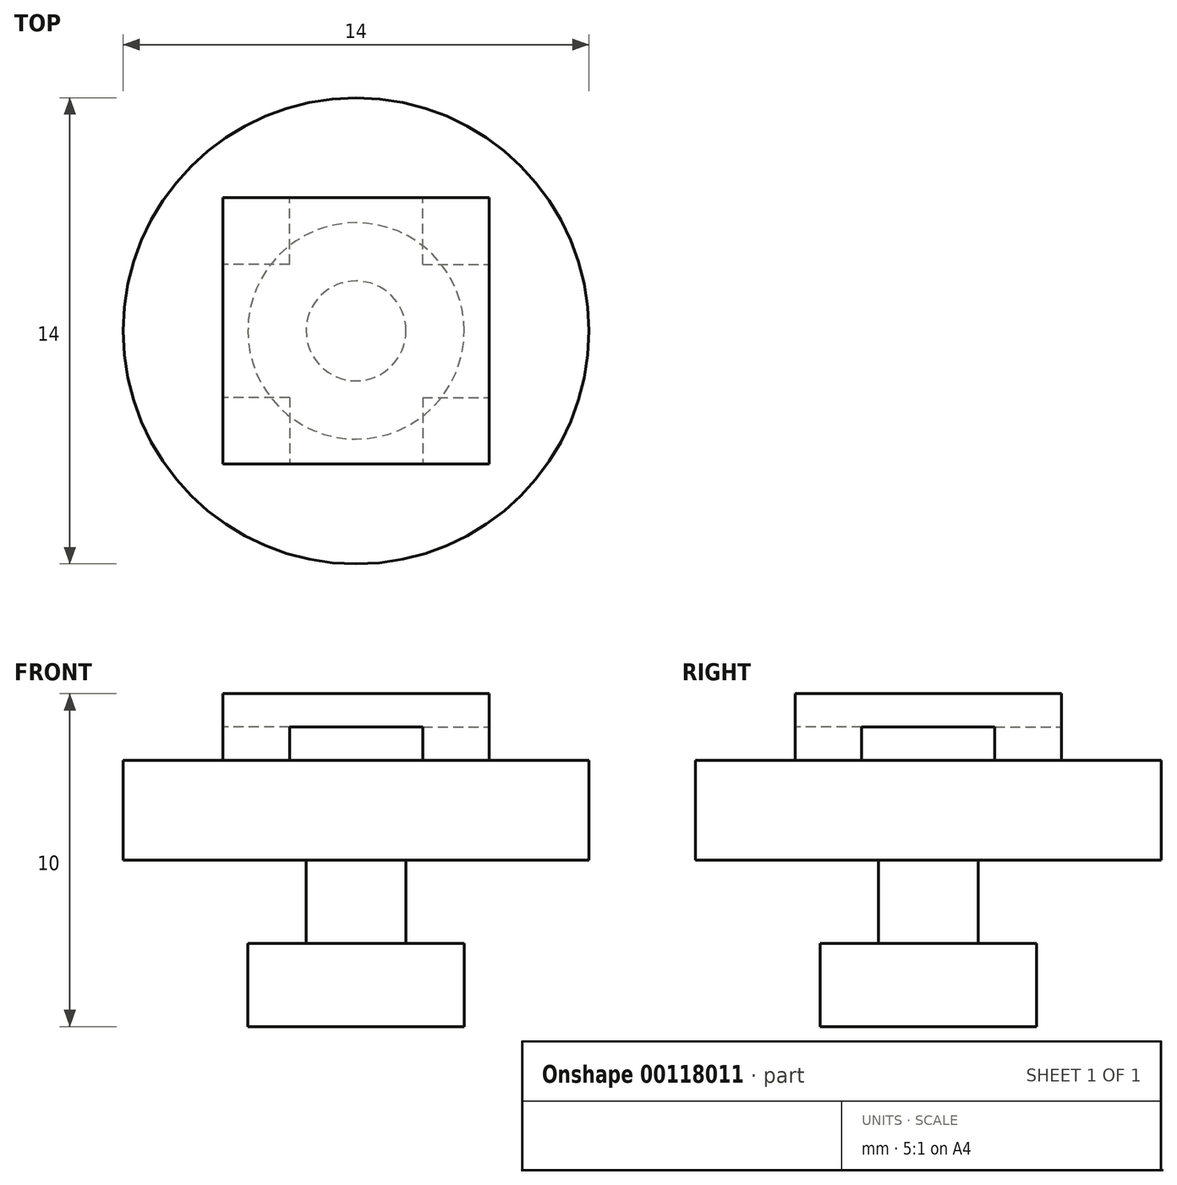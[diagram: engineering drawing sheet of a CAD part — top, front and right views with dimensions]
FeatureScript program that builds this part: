
annotation { "Feature Type Name" : "Feature", "Feature Type Description" : "" }
export const myFeature = defineFeature(function(context is Context, id is Id, definition is map)
    precondition{}
    {
        {
            var Q0;
            Q0=qCreatedBy(makeId("Top.planeOp"),FACE);
            var sketch = newSketch(context, id + "F0", { "sketchPlane" : qUnion([Q0])});
            skCircle(sketch, "E0", {"center": v(-13.15, -17.08) * mm, "radius": 3.25 * mm});
            skSolve(sketch);
        }
        {
            var Q0;
            Q0=makeQuery(id+"F0.imprint","IMPRINT",FACE,{"disambiguationData":[TD([[makeQuery(id+"F0.imprint","IMPRINT",EDGE,{"derivedFrom":sQuery(id+"F0.wireOp",EDGE,"E0")}),1.0]])]});
            extrude(context, id + "F1", {"entities" : qUnion([Q0]), "depth" : 2.5 * mm});
        }
        {
            var Q0;
            Q0=makeQuery(id+"F1.opExtrude","CAP_FACE",FACE,{"disambiguationData":[OSD([sQuery(id+"F0.wireOp",EDGE,"E0")])],"isStart":false});
            var sketch = newSketch(context, id + "F2", { "sketchPlane" : qUnion([Q0])});
            skCircle(sketch, "E1", {"center": v(-13.15, -17.08) * mm, "radius": 1.5 * mm});
            skSolve(sketch);
        }
        {
            var Q0;
            Q0=makeQuery(id+"F2.imprint","IMPRINT",FACE,{"disambiguationData":[TD([[makeQuery(id+"F2.imprint","IMPRINT",EDGE,{"derivedFrom":sQuery(id+"F2.wireOp",EDGE,"E1")}),1.0]])]});
            extrude(context, id + "F3", {"entities" : qUnion([Q0]), "operationType" : NewBodyOperationType.ADD, "depth" : 2.5 * mm});
        }
        {
            var Q0;
            Q0=makeQuery(id+"F3.opExtrude","CAP_FACE",FACE,{"disambiguationData":[OSD([sQuery(id+"F2.wireOp",EDGE,"E1")])],"isStart":false});
            var sketch = newSketch(context, id + "F4", { "sketchPlane" : qUnion([Q0])});
            skCircle(sketch, "E2", {"center": v(-13.15, -17.08) * mm, "radius": 7 * mm});
            skSolve(sketch);
        }
        {
            var Q0;
            Q0=makeQuery(id+"F4.imprint","IMPRINT",FACE,{"disambiguationData":[TD([[makeQuery(id+"F4.imprint","IMPRINT",EDGE,{"derivedFrom":sQuery(id+"F4.wireOp",EDGE,"E2")}),1.0]])]});
            extrude(context, id + "F5", {"entities" : qUnion([Q0]), "operationType" : NewBodyOperationType.ADD, "depth" : 3 * mm});
        }
        {
            var Q0;
            Q0=makeQuery(id+"F3.opExtrude","CAP_FACE",FACE,{"disambiguationData":[OSD([sQuery(id+"F2.wireOp",EDGE,"E1")])],"isStart":false});
            var sketch = newSketch(context, id + "F6", { "sketchPlane" : qUnion([Q0])});
            skCircle(sketch, "E3", {"center": v(-13.15, -17.08) * mm, "radius": 1.5 * mm});
            skSolve(sketch);
        }
        {
            var Q0;
            Q0=makeQuery(id+"F6.imprint","IMPRINT",FACE,{"disambiguationData":[TD([[makeQuery(id+"F6.imprint","IMPRINT",EDGE,{"derivedFrom":sQuery(id+"F6.wireOp",EDGE,"E3")}),1.0]])]});
            extrude(context, id + "F7", {"entities" : qUnion([Q0]), "operationType" : NewBodyOperationType.ADD, "depth" : 3 * mm});
        }
        {
            var Q0;
            Q0=makeQuery(id+"F7.boolean.opBoolean","MERGE",FACE,{"derivedFrom":[makeQuery(id+"F5.opExtrude","CAP_FACE",FACE,{"disambiguationData":[OSD([sQuery(id+"F2.wireOp",EDGE,"E1"),sQuery(id+"F4.wireOp",EDGE,"E2")])],"isStart":false}),makeQuery(id+"F7.opExtrude","CAP_FACE",FACE,{"disambiguationData":[OSD([sQuery(id+"F6.wireOp",EDGE,"E3")])],"isStart":false})]});
            var sketch = newSketch(context, id + "F8", { "sketchPlane" : qUnion([Q0])});
            skLineSegment(sketch, "E4.bottom", {"start": v(-15.15, -19.08) * mm, "end": v(-17.15, -19.08) * mm});
            skLineSegment(sketch, "E4.top", {"start": v(-15.15, -21.08) * mm, "end": v(-17.15, -21.08) * mm});
            skLineSegment(sketch, "E4.left", {"start": v(-15.15, -19.08) * mm, "end": v(-15.15, -21.08) * mm});
            skLineSegment(sketch, "E4.right", {"start": v(-17.15, -19.08) * mm, "end": v(-17.15, -21.08) * mm});
            skLineSegment(sketch, "E5.bottom", {"start": v(-11.15, -15.08) * mm, "end": v(-9.15, -15.08) * mm});
            skLineSegment(sketch, "E5.top", {"start": v(-11.15, -13.08) * mm, "end": v(-9.15, -13.08) * mm});
            skLineSegment(sketch, "E5.left", {"start": v(-11.15, -15.08) * mm, "end": v(-11.15, -13.08) * mm});
            skLineSegment(sketch, "E5.right", {"start": v(-9.15, -15.08) * mm, "end": v(-9.15, -13.08) * mm});
            skLineSegment(sketch, "E6.bottom", {"start": v(-15.15, -15.08) * mm, "end": v(-17.15, -15.08) * mm});
            skLineSegment(sketch, "E6.top", {"start": v(-15.15, -13.08) * mm, "end": v(-17.15, -13.08) * mm});
            skLineSegment(sketch, "E6.left", {"start": v(-15.15, -15.08) * mm, "end": v(-15.15, -13.08) * mm});
            skLineSegment(sketch, "E6.right", {"start": v(-17.15, -15.08) * mm, "end": v(-17.15, -13.08) * mm});
            skLineSegment(sketch, "E7.bottom", {"start": v(-11.15, -19.08) * mm, "end": v(-9.15, -19.08) * mm});
            skLineSegment(sketch, "E7.top", {"start": v(-11.15, -21.08) * mm, "end": v(-9.15, -21.08) * mm});
            skLineSegment(sketch, "E7.left", {"start": v(-11.15, -19.08) * mm, "end": v(-11.15, -21.08) * mm});
            skLineSegment(sketch, "E7.right", {"start": v(-9.15, -19.08) * mm, "end": v(-9.15, -21.08) * mm});
            skLineSegment(sketch, "E8", {"start": v(-13.15, -17.08) * mm, "end": v(-15.15, -17.08) * mm, "construction": true});
            skLineSegment(sketch, "E9", {"start": v(-13.15, -17.08) * mm, "end": v(-11.15, -17.08) * mm, "construction": true});
            skSolve(sketch);
        }
        {
            var Q0;
            Q0=makeQuery(id+"F8.imprint","IMPRINT",FACE,{"disambiguationData":[TD([[makeQuery(id+"F8.imprint","IMPRINT",EDGE,{"derivedFrom":sQuery(id+"F8.wireOp",EDGE,"E6.bottom")}),-1.0]])]});
            var Q1;
            Q1=makeQuery(id+"F8.imprint","IMPRINT",FACE,{"disambiguationData":[TD([[makeQuery(id+"F8.imprint","IMPRINT",EDGE,{"derivedFrom":sQuery(id+"F8.wireOp",EDGE,"E5.bottom")}),1.0]])]});
            var Q2;
            Q2=makeQuery(id+"F8.imprint","IMPRINT",FACE,{"disambiguationData":[TD([[makeQuery(id+"F8.imprint","IMPRINT",EDGE,{"derivedFrom":sQuery(id+"F8.wireOp",EDGE,"E7.bottom")}),-1.0]])]});
            var Q3;
            Q3=makeQuery(id+"F8.imprint","IMPRINT",FACE,{"disambiguationData":[TD([[makeQuery(id+"F8.imprint","IMPRINT",EDGE,{"derivedFrom":sQuery(id+"F8.wireOp",EDGE,"E4.bottom")}),1.0]])]});
            extrude(context, id + "F9", {"entities" : qUnion([Q0, Q1, Q2, Q3]), "operationType" : NewBodyOperationType.ADD, "depth" : 2 * mm});
        }
        {
            var Q0;
            Q0=makeQuery(id+"F9.opExtrude","CAP_FACE",FACE,{"disambiguationData":[OSD([sQuery(id+"F8.wireOp",EDGE,"E6.bottom"),sQuery(id+"F8.wireOp",EDGE,"E6.top"),sQuery(id+"F8.wireOp",EDGE,"E6.left"),sQuery(id+"F8.wireOp",EDGE,"E6.right")])],"isStart":false});
            var sketch = newSketch(context, id + "F10", { "sketchPlane" : qUnion([Q0])});
            skLineSegment(sketch, "E10.bottom", {"start": v(-17.15, -13.08) * mm, "end": v(-9.15, -13.08) * mm});
            skLineSegment(sketch, "E10.top", {"start": v(-17.15, -21.08) * mm, "end": v(-9.15, -21.08) * mm});
            skLineSegment(sketch, "E10.left", {"start": v(-17.15, -13.08) * mm, "end": v(-17.15, -21.08) * mm});
            skLineSegment(sketch, "E10.right", {"start": v(-9.15, -13.08) * mm, "end": v(-9.15, -21.08) * mm});
            skSolve(sketch);
        }
        {
            var Q0;
            {var subQ2=sQuery(id+"F10.wireOp",EDGE,"E10.top");Q0=makeQuery(id+"F10.imprint","IMPRINT",FACE,{"disambiguationData":[TD([[makeQuery(id+"F10.imprint","IMPRINT",EDGE,{"derivedFrom":subQ2}),1.0]])]});}
            extrude(context, id + "F11", {"entities" : qUnion([Q0]), "operationType" : NewBodyOperationType.ADD, "oppositeDirection" : true, "depth" : 1 * mm});
        }
    });
